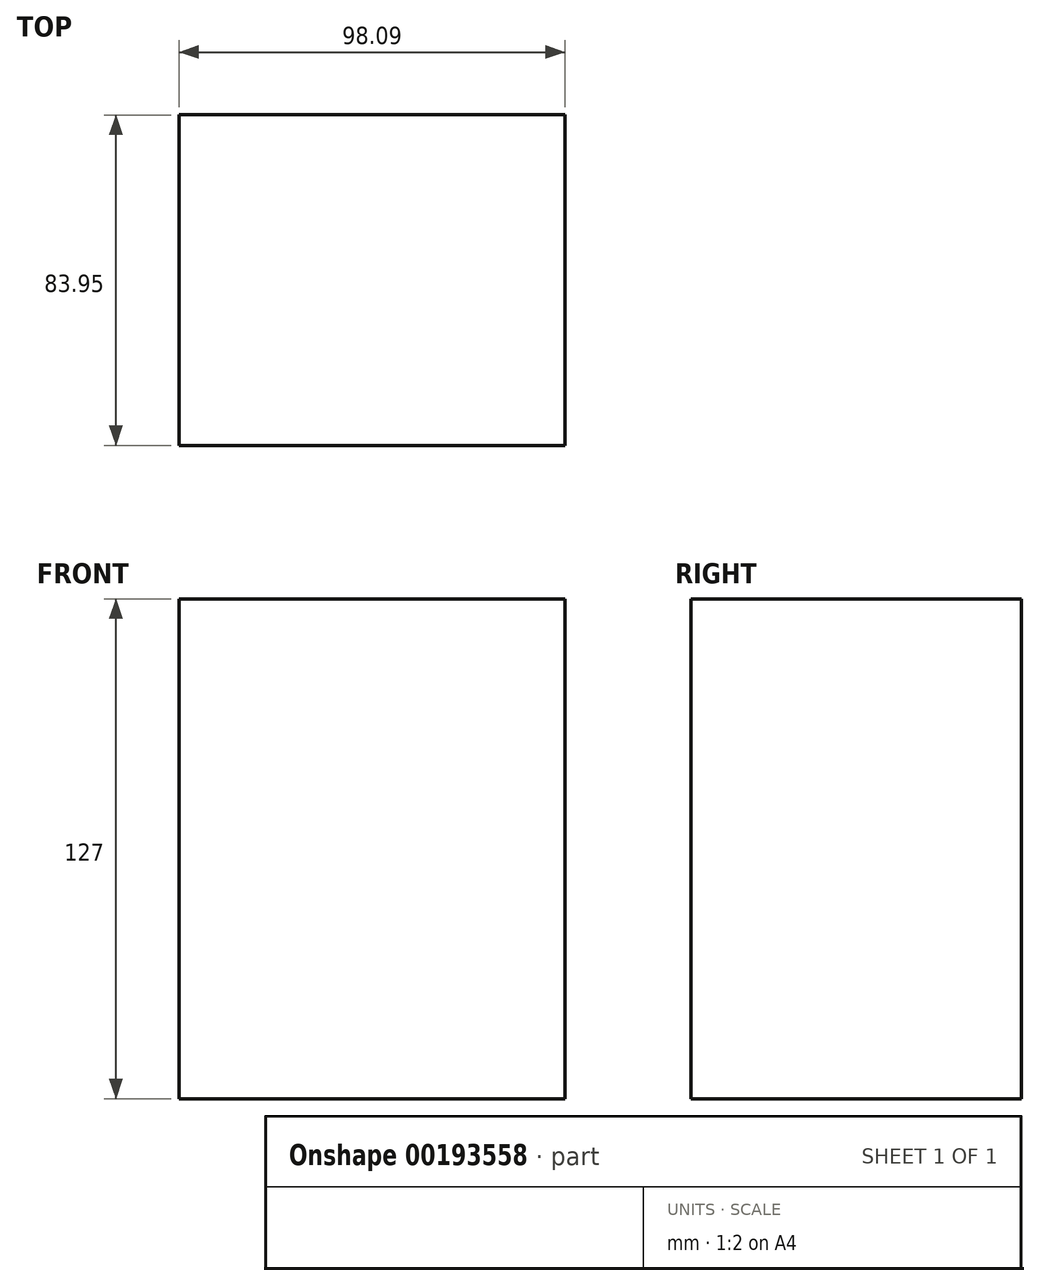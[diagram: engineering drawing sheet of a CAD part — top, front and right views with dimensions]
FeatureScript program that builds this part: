
annotation { "Feature Type Name" : "Feature", "Feature Type Description" : "" }
export const myFeature = defineFeature(function(context is Context, id is Id, definition is map)
    precondition{}
    {
        {
            var Q0;
            Q0=qCreatedBy(makeId("Top.planeOp"),FACE);
            var sketch = newSketch(context, id + "F0", { "sketchPlane" : qUnion([Q0])});
            skLineSegment(sketch, "E0.bottom", {"start": v(-46.4, 46.17) * mm, "end": v(51.7, 46.17) * mm});
            skLineSegment(sketch, "E0.top", {"start": v(-46.4, -37.78) * mm, "end": v(51.7, -37.78) * mm});
            skLineSegment(sketch, "E0.left", {"start": v(-46.4, 46.17) * mm, "end": v(-46.4, -37.78) * mm});
            skLineSegment(sketch, "E0.right", {"start": v(51.7, 46.17) * mm, "end": v(51.7, -37.78) * mm});
            skSolve(sketch);
        }
        {
            var Q0;
            Q0 = qSketchRegion(id + "F0", true);
            extrude(context, id + "F1", {"entities" : qUnion([Q0]), "depth" : 127 * mm});
        }
    });
